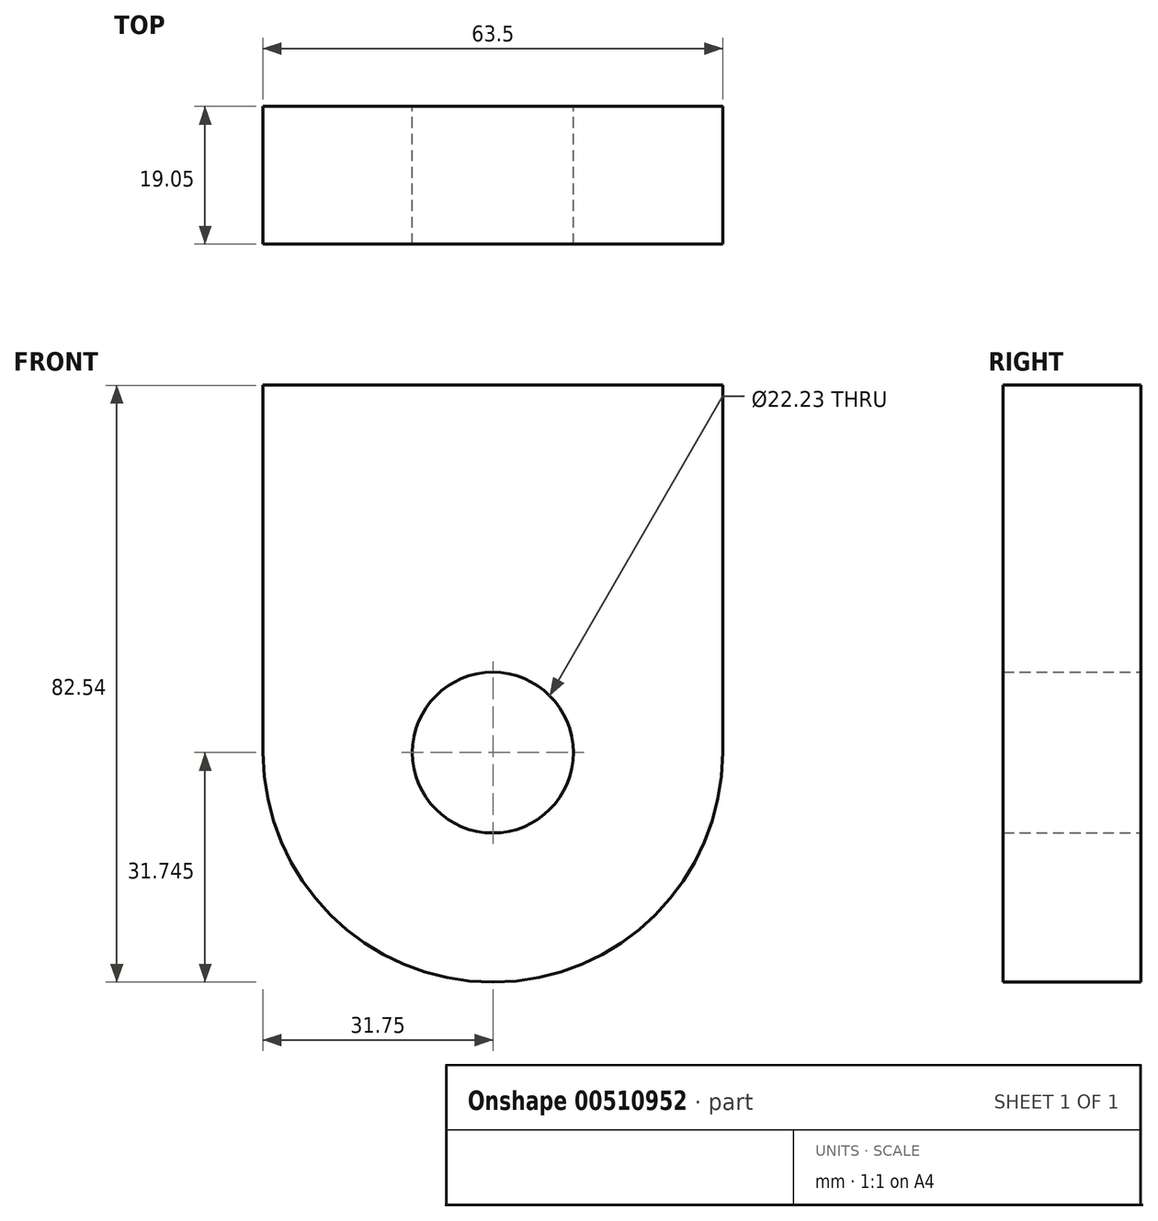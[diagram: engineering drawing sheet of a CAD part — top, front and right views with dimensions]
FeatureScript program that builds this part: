
annotation { "Feature Type Name" : "Feature", "Feature Type Description" : "" }
export const myFeature = defineFeature(function(context is Context, id is Id, definition is map)
    precondition{}
    {
        {
            var Q0;
            Q0=qCreatedBy(makeId("Front.planeOp"),FACE);
            var sketch = newSketch(context, id + "F0", { "sketchPlane" : qUnion([Q0])});
            skLineSegment(sketch, "E0.bottom", {"start": v(0, -41.28) * mm, "end": v(0, -41.28) * mm});
            skLineSegment(sketch, "E0.top", {"start": v(-31.75, 41.28) * mm, "end": v(31.75, 41.28) * mm});
            skLineSegment(sketch, "E0.left", {"start": v(-31.75, -9.53) * mm, "end": v(-31.75, 41.28) * mm});
            skLineSegment(sketch, "E0.right", {"start": v(31.75, -9.53) * mm, "end": v(31.75, 41.28) * mm});
            skPoint(sketch, "E0.middle", {"position": v(0, 0) * mm});
            skPoint(sketch, "E1", {"position": v(0, -9.52) * mm});
            skPoint(sketch, "E2.visualSharp", {"position": v(31.75, -41.28) * mm});
            skArc(sketch, "E2.filletArc", {"start": v(0, -41.28) * mm, "mid": v(22.45, -31.98) * mm, "end": v(31.75, -9.53) * mm});
            skPoint(sketch, "E3.visualSharp", {"position": v(-31.75, -41.28) * mm});
            skArc(sketch, "E3.filletArc", {"start": v(-31.75, -9.53) * mm, "mid": v(-22.45, -31.98) * mm, "end": v(0, -41.28) * mm});
            skCircle(sketch, "E4", {"center": v(0, -9.52) * mm, "radius": 11.11 * mm});
            skSolve(sketch);
        }
        {
            var Q0;
            Q0=makeQuery(id+"F0.imprint","IMPRINT",FACE,{"disambiguationData":[TD([[makeQuery(id+"F0.imprint","IMPRINT",EDGE,{"derivedFrom":sQuery(id+"F0.wireOp",EDGE,"E0.top")}),-1.0]])]});
            extrude(context, id + "F1", {"entities" : qUnion([Q0]), "depth" : 19.05 * mm, "offsetDistance" : 25.4 * mm});
        }
    });
